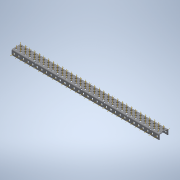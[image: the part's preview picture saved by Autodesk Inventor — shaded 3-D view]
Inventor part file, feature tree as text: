
AUTODESK INVENTOR PART (.ipt)
format: ipt  version: 2020 (Build 240168000, 168)  size: 2,292,736 bytes
history: native  units: in
note: dims shown in document units (in); Inventor stores cm internally (conversion verified against a paired STEP export)
features: other x166, pattern_linear x3, sheet_metal_op x1, extrude x1, plane x1, split x1, imported_body x1, sketch x1
ambient origin geometry x8: Origin, YZ Plane, XZ Plane, XY Plane, X Axis, Y Axis, Z Axis, Center Point
bodies: Body1 (feature_tree)
feature tree (175):
  sheet_metal_op  "Fold1"
  other  "C-Channel"
  extrude  "length cut"  Depth=0.5in
  other  "top axis"
  other  "inner axis"
  other  "front axis"
  other  "back axis"
  pattern_linear  "top axes"  Spacing1=0.5in  [1 undecoded]
  pattern_linear  "inner axes"  Spacing1=0.5in  [1 undecoded]
  pattern_linear  "horiz axes"  Spacing1=-17.5in  [1 undecoded]
  other  "right plane"
  plane  "Work Plane3"
  split  "Split1"
  imported_body  "Base1"
  sketch  "Sketch1"  dims[d1=0.0in d4=0.5in d5=0.7874in d7=0.5in d10=0.5in d13=0.5in d14=-17.5in d15=0.0in d16=0.0in d17=0.0in d18=0.0in d19=0.0in]
  other  "Work Point1"
  other  "Work Point2"
  other  "Work Point3"
  other  "Work Point4"
  other  "Work Axis5"
  other  "Work Axis6"
  other  "Work Axis7"
  other  "Work Axis8"
  other  "Work Axis11"
  other  "Work Axis12"
  other  "Work Axis13"
  other  "Work Axis14"
  other  "Work Axis15"
  other  "Work Axis18"
  other  "Work Axis19"
  other  "Work Axis20"
  other  "Work Axis23"
  other  "Work Axis24"
  other  "Work Axis25"
  other  "Work Axis26"
  other  "Work Axis30"
  other  "Work Axis31"
  other  "Work Axis32"
  other  "Work Axis33"
  other  "left plane"
  other  "Work Axis37"
  other  "Work Axis38"
  other  "Work Axis39"
  other  "Work Axis40"
  other  "Work Axis41"
  other  "Work Axis42"
  other  "Work Axis43"
  other  "Work Axis44"
  other  "Work Axis45"
  other  "Work Axis46"
  other  "Work Axis47"
  other  "Work Axis48"
  other  "Work Axis49"
  other  "Work Axis50"
  other  "Work Axis51"
  other  "Work Axis52"
  other  "Work Axis53"
  other  "Work Axis54"
  other  "Work Axis55"
  other  "Work Axis56"
  other  "Work Axis57"
  other  "Work Axis58"
  other  "Work Axis59"
  other  "Work Axis60"
  other  "Work Axis61"
  other  "Work Axis62"
  other  "Work Axis63"
  other  "Work Axis64"
  other  "Work Axis65"
  other  "Work Axis66"
  other  "Work Axis67"
  other  "Work Axis68"
  other  "Work Axis69"
  other  "Work Axis70"
  other  "Work Axis71"
  other  "Work Axis72"
  other  "Work Axis73"
  other  "Work Axis74"
  other  "Work Axis75"
  other  "Work Axis76"
  other  "Work Axis77"
  other  "Work Axis78"
  other  "Work Axis79"
  other  "Work Axis80"
  other  "Work Axis81"
  other  "Work Axis82"
  other  "Work Axis83"
  other  "Work Axis84"
  other  "Work Axis85"
  other  "Work Axis86"
  other  "Work Axis87"
  other  "Work Axis88"
  other  "Work Axis89"
  other  "Work Axis90"
  other  "Work Axis91"
  other  "Work Axis92"
  other  "Work Axis93"
  other  "Work Axis94"
  other  "Work Axis95"
  other  "Work Axis96"
  other  "Work Axis97"
  other  "Work Axis98"
  other  "Work Axis99"
  other  "Work Axis100"
  other  "Work Axis101"
  other  "Work Axis102"
  other  "Work Axis103"
  other  "Work Axis104"
  other  "Work Axis105"
  other  "Work Axis106"
  other  "Work Axis107"
  other  "Work Axis108"
  other  "Work Axis109"
  other  "Work Axis110"
  other  "Work Axis111"
  other  "Work Axis112"
  other  "Work Axis113"
  other  "Work Axis114"
  other  "Work Axis115"
  other  "Work Axis116"
  other  "Work Axis117"
  other  "Work Axis118"
  other  "Work Axis119"
  other  "Work Axis120"
  other  "Work Axis121"
  other  "Work Axis122"
  other  "Work Axis123"
  other  "Work Axis124"
  other  "Work Axis125"
  other  "Work Axis126"
  other  "Work Axis127"
  other  "Work Axis128"
  other  "Work Axis129"
  other  "Work Axis130"
  other  "Work Axis131"
  other  "Work Axis132"
  other  "Work Axis133"
  other  "Work Axis134"
  other  "Work Axis135"
  other  "Work Axis136"
  other  "Work Axis137"
  other  "Work Axis138"
  other  "Work Axis139"
  other  "Work Axis140"
  other  "Work Axis141"
  other  "Work Axis142"
  other  "Work Axis143"
  other  "Work Axis144"
  other  "Work Axis145"
  other  "Work Axis146"
  other  "Work Axis147"
  other  "Work Axis148"
  other  "Work Axis149"
  other  "Work Axis150"
  other  "Work Axis151"
  other  "Work Axis152"
  other  "Work Axis153"
  other  "Work Axis154"
  other  "Work Axis155"
  other  "Work Axis156"
  other  "Work Axis157"
  other  "Work Axis158"
  other  "Work Axis159"
  other  "Work Axis163"
  other  "Work Axis164"
  other  "Work Axis165"
  other  "Work Axis169"
  other  "Work Axis170"
  other  "Work Axis171"
  other  "Work Axis175"
  other  "Work Axis176"
  other  "Work Axis177"
  other  "Work Axis181"
  other  "Work Axis182"
  other  "Work Axis183"
note: 3 required parameter values undecoded (feature->parameter linkage not recoverable at this tier; creation-order binding heuristic only, values carry confidence <= 0.55)
